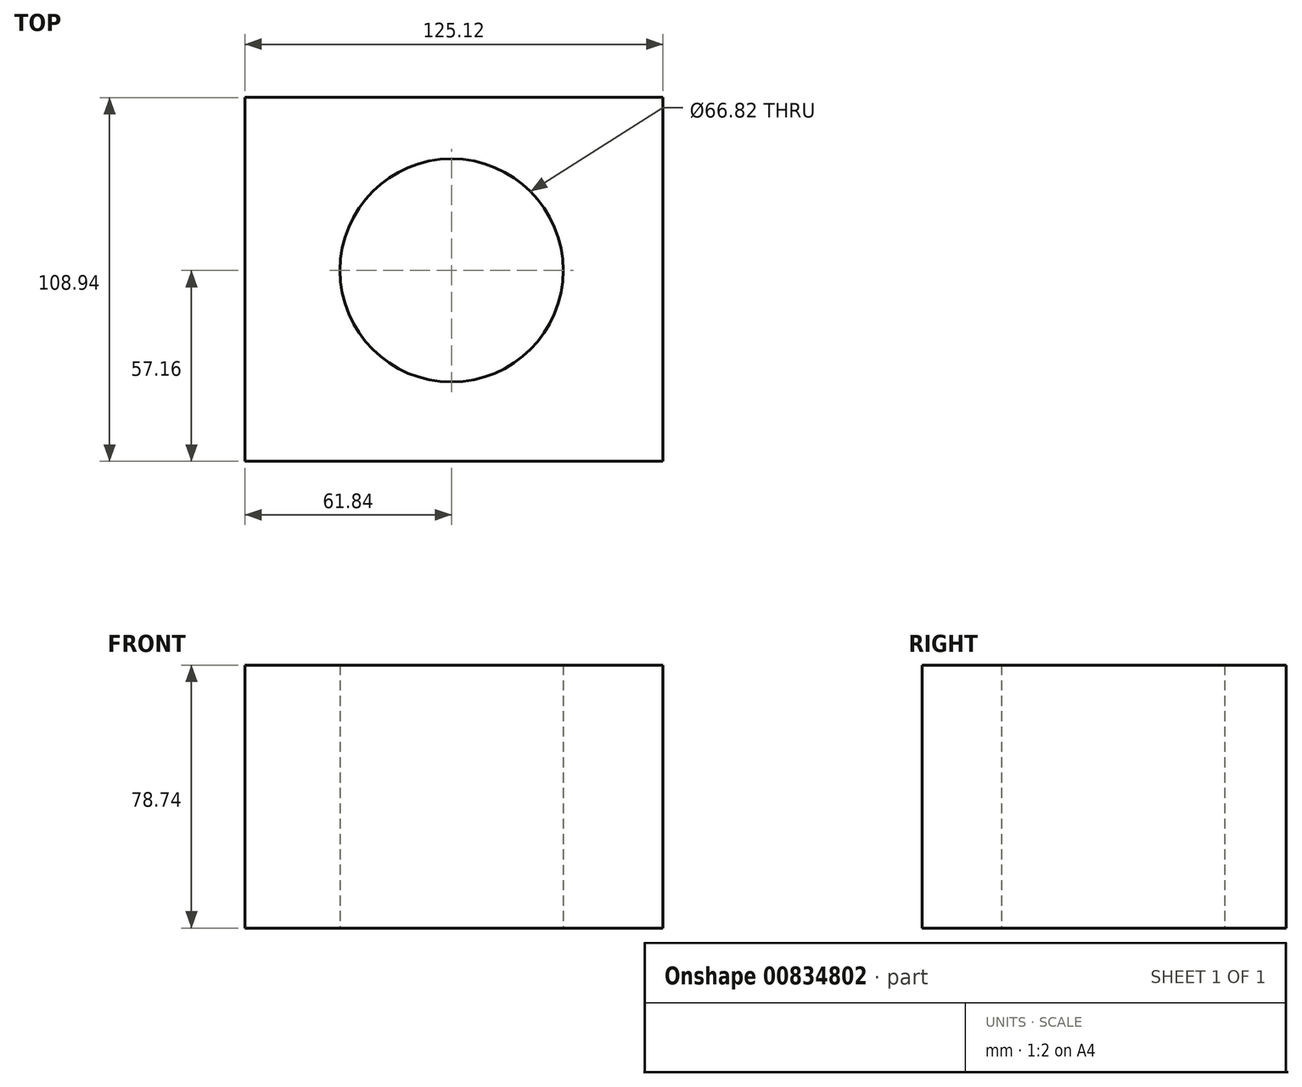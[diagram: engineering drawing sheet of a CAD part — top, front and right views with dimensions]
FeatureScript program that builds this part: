
annotation { "Feature Type Name" : "Feature", "Feature Type Description" : "" }
export const myFeature = defineFeature(function(context is Context, id is Id, definition is map)
    precondition{}
    {
        {
            var Q0;
            Q0=qCreatedBy(makeId("Top.planeOp"),FACE);
            var sketch = newSketch(context, id + "F0", { "sketchPlane" : qUnion([Q0])});
            skCircle(sketch, "E0", {"center": v(0, 0) * mm, "radius": 33.41 * mm});
            skLineSegment(sketch, "E1.bottom", {"start": v(-61.84, 51.78) * mm, "end": v(63.28, 51.78) * mm});
            skLineSegment(sketch, "E1.top", {"start": v(-61.84, -57.16) * mm, "end": v(63.28, -57.16) * mm});
            skLineSegment(sketch, "E1.left", {"start": v(-61.84, 51.78) * mm, "end": v(-61.84, -57.16) * mm});
            skLineSegment(sketch, "E1.right", {"start": v(63.28, 51.78) * mm, "end": v(63.28, -57.16) * mm});
            skSolve(sketch);
        }
        {
            var Q0;
            Q0=makeQuery(id+"F0.imprint","IMPRINT",FACE,{"disambiguationData":[TD([[makeQuery(id+"F0.imprint","IMPRINT",EDGE,{"derivedFrom":sQuery(id+"F0.wireOp",EDGE,"E0")}),-1.0]])]});
            extrude(context, id + "F1", {"entities" : qUnion([Q0]), "depth" : 78.74 * mm, "offsetDistance" : 25.4 * mm});
        }
    });
